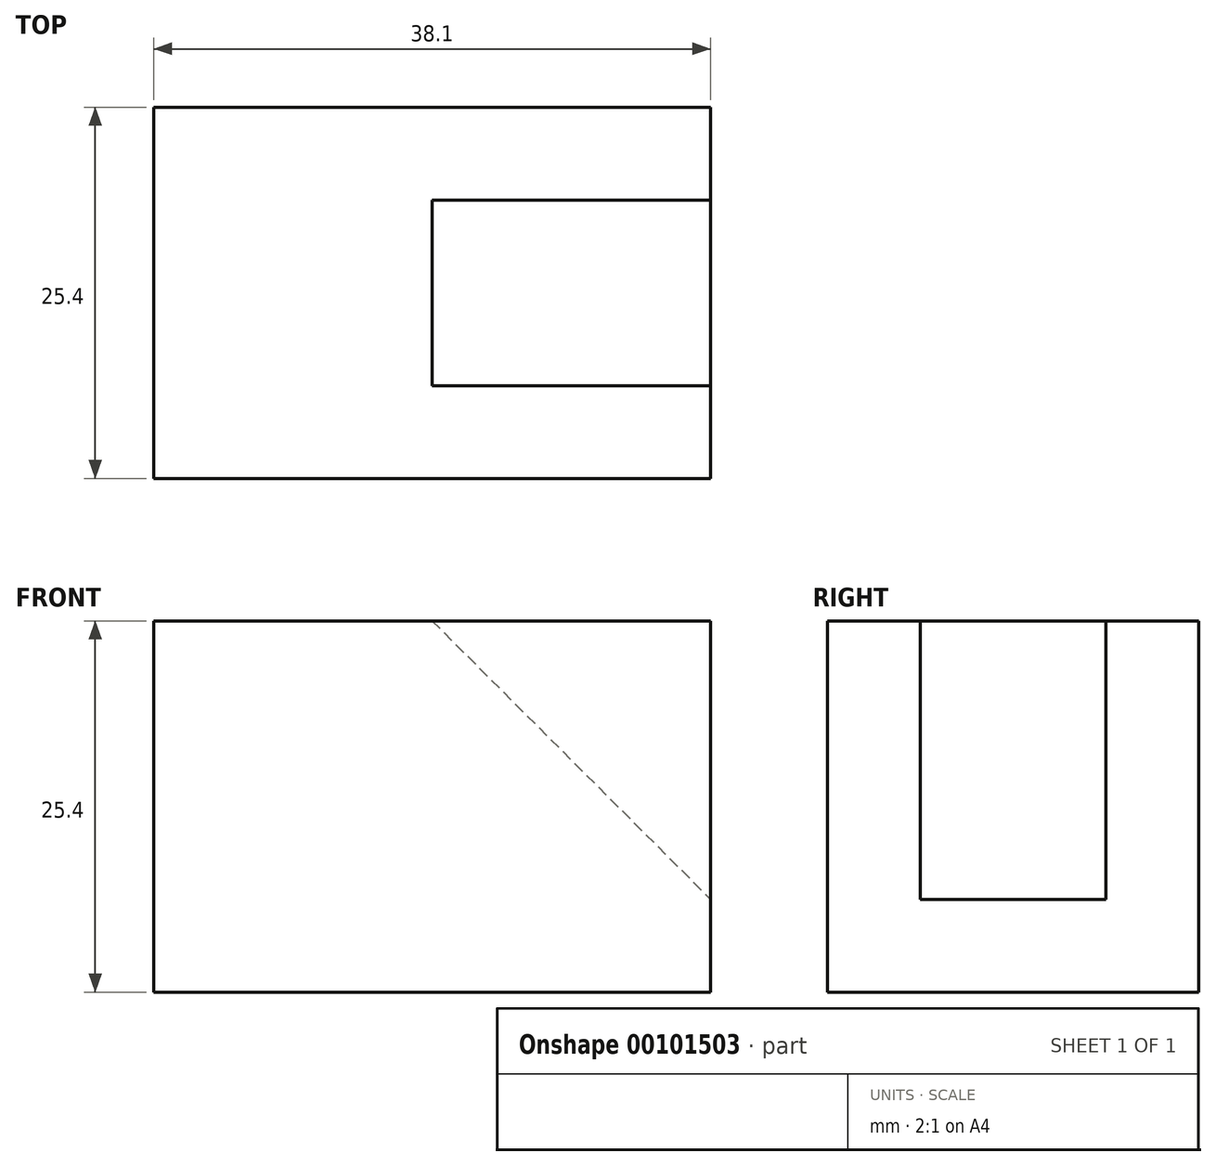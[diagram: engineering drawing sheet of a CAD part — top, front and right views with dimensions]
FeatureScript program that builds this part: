
annotation { "Feature Type Name" : "Feature", "Feature Type Description" : "" }
export const myFeature = defineFeature(function(context is Context, id is Id, definition is map)
    precondition{}
    {
        {
            var Q0;
            Q0=qCreatedBy(makeId("Front.planeOp"),FACE);
            var sketch = newSketch(context, id + "F0", { "sketchPlane" : qUnion([Q0])});
            skLineSegment(sketch, "E0.bottom", {"start": v(0, 0) * mm, "end": v(38.1, 0) * mm});
            skLineSegment(sketch, "E0.top", {"start": v(0, 25.4) * mm, "end": v(38.1, 25.4) * mm});
            skLineSegment(sketch, "E0.left", {"start": v(0, 0) * mm, "end": v(0, 25.4) * mm});
            skLineSegment(sketch, "E0.right", {"start": v(38.1, 0) * mm, "end": v(38.1, 25.4) * mm});
            skSolve(sketch);
        }
        {
            var Q0;
            Q0 = qSketchRegion(id + "F0", true);
            extrude(context, id + "F1", {"entities" : qUnion([Q0]), "endBound" : BoundingType.SYMMETRIC, "depth" : 25.4 * mm});
        }
        {
            var Q0;
            Q0=qCreatedBy(makeId("Front.planeOp"),FACE);
            var sketch = newSketch(context, id + "F2", { "sketchPlane" : qUnion([Q0])});
            skLineSegment(sketch, "E1", {"start": v(19.05, 25.4) * mm, "end": v(38.1, 6.35) * mm});
            skLineSegment(sketch, "E2", {"start": v(38.1, 6.35) * mm, "end": v(38.1, 25.4) * mm});
            skLineSegment(sketch, "E3", {"start": v(38.1, 25.4) * mm, "end": v(19.05, 25.4) * mm});
            skSolve(sketch);
        }
        {
            var Q0;
            Q0 = qSketchRegion(id + "F2", true);
            extrude(context, id + "F3", {"entities" : qUnion([Q0]), "operationType" : NewBodyOperationType.REMOVE, "endBound" : BoundingType.SYMMETRIC, "depth" : 12.7 * mm});
        }
    });
